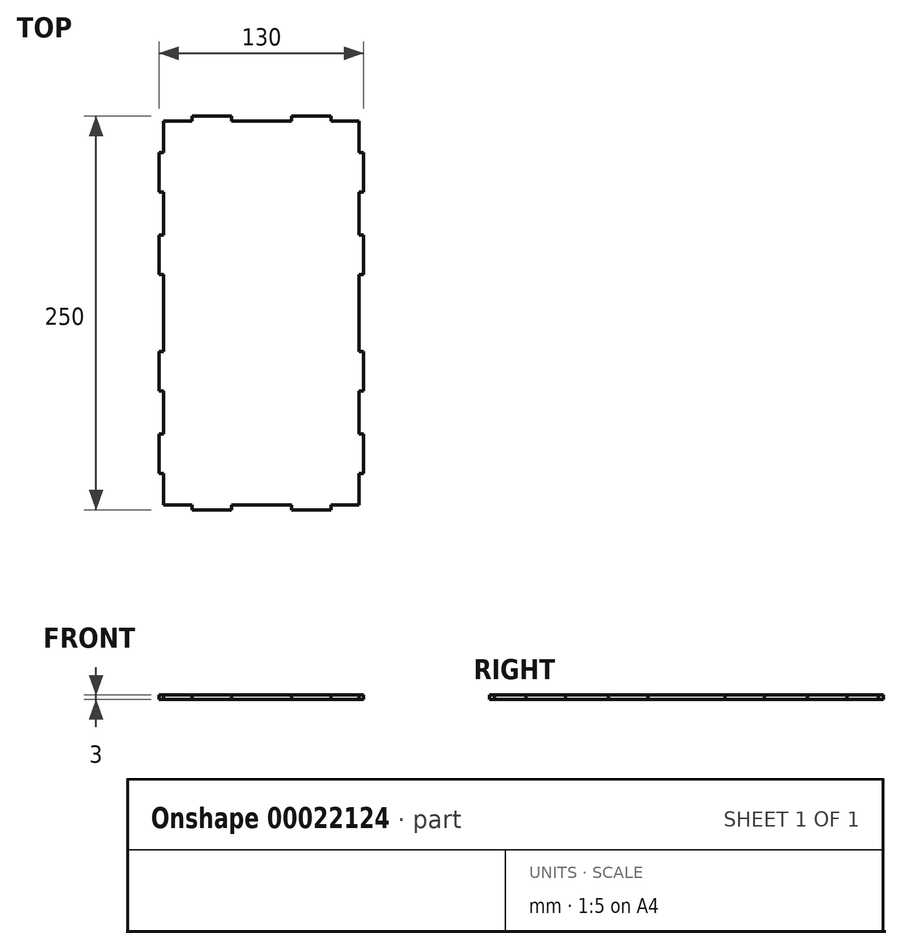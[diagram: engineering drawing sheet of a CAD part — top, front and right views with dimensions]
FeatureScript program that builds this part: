
annotation { "Feature Type Name" : "Feature", "Feature Type Description" : "" }
export const myFeature = defineFeature(function(context is Context, id is Id, definition is map)
    precondition{}
    {
        {
            var Q0;
            Q0=qCreatedBy(makeId("Top.planeOp"),FACE);
            var sketch = newSketch(context, id + "F0", { "sketchPlane" : qUnion([Q0])});
            skLineSegment(sketch, "E0.bottom", {"start": v(-162.5, 101.91) * mm, "end": v(-159.5, 101.91) * mm});
            skLineSegment(sketch, "E0.top", {"start": v(-162.5, 76.91) * mm, "end": v(-159.5, 76.91) * mm});
            skLineSegment(sketch, "E1.bottom", {"start": v(-162.5, 49.42) * mm, "end": v(-159.5, 49.42) * mm});
            skLineSegment(sketch, "E1.top", {"start": v(-162.5, 24.42) * mm, "end": v(-159.5, 24.42) * mm});
            skLineSegment(sketch, "E2.MirrorCS", {"start": v(-32.5, 76.91) * mm, "end": v(-35.5, 76.91) * mm});
            skLineSegment(sketch, "E3.MirrorCS", {"start": v(-32.5, 101.91) * mm, "end": v(-35.5, 101.91) * mm});
            skLineSegment(sketch, "E4.MirrorCS", {"start": v(-32.5, 49.42) * mm, "end": v(-35.5, 49.42) * mm});
            skLineSegment(sketch, "E5.MirrorCS", {"start": v(-32.5, 24.42) * mm, "end": v(-35.5, 24.42) * mm});
            skLineSegment(sketch, "E6.MirrorCS", {"start": v(-162.5, -49.42) * mm, "end": v(-159.5, -49.42) * mm});
            skLineSegment(sketch, "E7.MirrorCS", {"start": v(-162.5, -24.42) * mm, "end": v(-159.5, -24.42) * mm});
            skLineSegment(sketch, "E8.MirrorCS", {"start": v(-162.5, -76.91) * mm, "end": v(-159.5, -76.91) * mm});
            skLineSegment(sketch, "E9.MirrorCS", {"start": v(-162.5, -101.91) * mm, "end": v(-159.5, -101.91) * mm});
            skLineSegment(sketch, "E10.MirrorCS", {"start": v(-32.5, -76.91) * mm, "end": v(-35.5, -76.91) * mm});
            skLineSegment(sketch, "E11.MirrorCS", {"start": v(-32.5, -49.42) * mm, "end": v(-35.5, -49.42) * mm});
            skLineSegment(sketch, "E12.MirrorCS", {"start": v(-32.5, -24.42) * mm, "end": v(-35.5, -24.42) * mm});
            skLineSegment(sketch, "E13.MirrorCS", {"start": v(-32.5, -101.91) * mm, "end": v(-35.5, -101.91) * mm});
            skLineSegment(sketch, "E14", {"start": v(-35.5, 122) * mm, "end": v(-35.5, 101.91) * mm});
            skLineSegment(sketch, "E15", {"start": v(-32.5, -101.91) * mm, "end": v(-32.5, -76.91) * mm});
            skLineSegment(sketch, "E16", {"start": v(-32.5, -49.42) * mm, "end": v(-32.5, -24.42) * mm});
            skLineSegment(sketch, "E17", {"start": v(-32.5, 24.42) * mm, "end": v(-32.5, 49.42) * mm});
            skLineSegment(sketch, "E18", {"start": v(-32.5, 76.91) * mm, "end": v(-32.5, 101.91) * mm});
            skLineSegment(sketch, "E19.trimOffspring", {"start": v(-35.5, 76.91) * mm, "end": v(-35.5, 49.42) * mm});
            skLineSegment(sketch, "E20.trimOffspring", {"start": v(-35.5, 24.42) * mm, "end": v(-35.5, -24.42) * mm});
            skLineSegment(sketch, "E21.trimOffspring", {"start": v(-35.5, -101.91) * mm, "end": v(-35.5, -122) * mm});
            skLineSegment(sketch, "E22.trimOffspring", {"start": v(-35.5, -49.42) * mm, "end": v(-35.5, -76.91) * mm});
            skLineSegment(sketch, "E23", {"start": v(-159.5, -122) * mm, "end": v(-159.5, -101.91) * mm});
            skLineSegment(sketch, "E24", {"start": v(-162.5, 101.91) * mm, "end": v(-162.5, 76.91) * mm});
            skLineSegment(sketch, "E25", {"start": v(-162.5, 49.42) * mm, "end": v(-162.5, 24.42) * mm});
            skLineSegment(sketch, "E26", {"start": v(-162.5, -24.42) * mm, "end": v(-162.5, -49.42) * mm});
            skLineSegment(sketch, "E27", {"start": v(-162.5, -76.91) * mm, "end": v(-162.5, -101.91) * mm});
            skPoint(sketch, "E28.MirrorCS.start.orphan", {"position": v(-159.5, -101.91) * mm});
            skLineSegment(sketch, "E29.trimOffspring", {"start": v(-159.5, -76.91) * mm, "end": v(-159.5, -49.42) * mm});
            skLineSegment(sketch, "E30.trimOffspring", {"start": v(-159.5, -24.42) * mm, "end": v(-159.5, 24.42) * mm});
            skLineSegment(sketch, "E31.trimOffspring", {"start": v(-159.5, 49.42) * mm, "end": v(-159.5, 76.91) * mm});
            skLineSegment(sketch, "E32.trimOffspring", {"start": v(-159.5, 101.91) * mm, "end": v(-159.5, 122) * mm});
            skLineSegment(sketch, "E33", {"start": v(-159.5, 0) * mm, "end": v(-35.5, 0) * mm, "construction": true});
            skLineSegment(sketch, "E34", {"start": v(-159.5, -122) * mm, "end": v(-141.6, -122) * mm});
            skLineSegment(sketch, "E35", {"start": v(-159.5, 122) * mm, "end": v(-141.6, 122) * mm});
            skLineSegment(sketch, "E36.top", {"start": v(-141.6, 125) * mm, "end": v(-116.62, 125) * mm});
            skLineSegment(sketch, "E36.left", {"start": v(-141.6, 122) * mm, "end": v(-141.6, 125) * mm});
            skLineSegment(sketch, "E36.right", {"start": v(-116.62, 122) * mm, "end": v(-116.62, 125) * mm});
            skLineSegment(sketch, "E37.trimOffspring", {"start": v(-116.62, 122) * mm, "end": v(-78.38, 122) * mm});
            skLineSegment(sketch, "E38", {"start": v(-97.5, -122) * mm, "end": v(-97.5, 122) * mm, "construction": true});
            skLineSegment(sketch, "E39.MirrorCS", {"start": v(-53.4, 125) * mm, "end": v(-78.38, 125) * mm});
            skLineSegment(sketch, "E40.MirrorCS", {"start": v(-53.4, 122) * mm, "end": v(-53.4, 125) * mm});
            skLineSegment(sketch, "E41.MirrorCS", {"start": v(-78.38, 122) * mm, "end": v(-78.38, 125) * mm});
            skLineSegment(sketch, "E42.trimOffspring", {"start": v(-53.4, 122) * mm, "end": v(-35.5, 122) * mm});
            skLineSegment(sketch, "E43.MirrorCS", {"start": v(-53.4, -125) * mm, "end": v(-78.38, -125) * mm});
            skLineSegment(sketch, "E44.MirrorCS", {"start": v(-141.6, -125) * mm, "end": v(-116.62, -125) * mm});
            skLineSegment(sketch, "E45.MirrorCS", {"start": v(-141.6, -122) * mm, "end": v(-141.6, -125) * mm});
            skLineSegment(sketch, "E46.MirrorCS", {"start": v(-116.62, -122) * mm, "end": v(-116.62, -125) * mm});
            skLineSegment(sketch, "E47.MirrorCS", {"start": v(-78.38, -122) * mm, "end": v(-78.38, -125) * mm});
            skLineSegment(sketch, "E48.MirrorCS", {"start": v(-53.4, -122) * mm, "end": v(-53.4, -125) * mm});
            skLineSegment(sketch, "E49.trimOffspring", {"start": v(-116.62, -122) * mm, "end": v(-78.38, -122) * mm});
            skLineSegment(sketch, "E50.trimOffspring", {"start": v(-53.4, -122) * mm, "end": v(-35.5, -122) * mm});
            skSolve(sketch);
        }
        {
            var Q0;
            Q0=makeQuery(id+"F0.imprint","IMPRINT",FACE,{"disambiguationData":[TD([[makeQuery(id+"F0.imprint","IMPRINT",EDGE,{"derivedFrom":sQuery(id+"F0.wireOp",EDGE,"E0.bottom")}),-1.0]])]});
            extrude(context, id + "F1", {"entities" : qUnion([Q0]), "depth" : 3 * mm});
        }
    });
